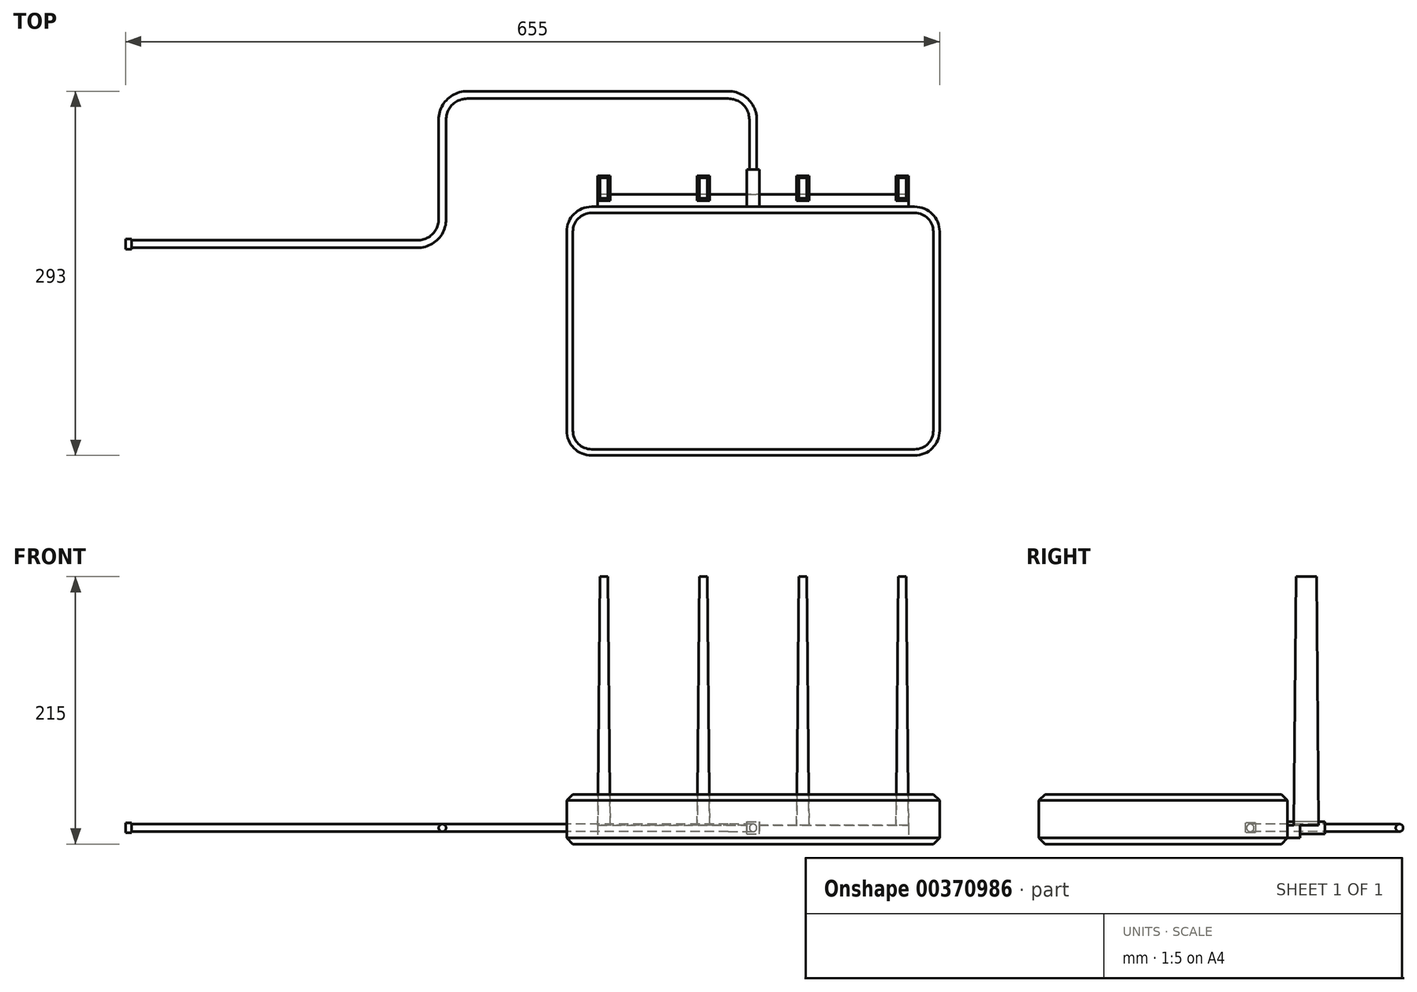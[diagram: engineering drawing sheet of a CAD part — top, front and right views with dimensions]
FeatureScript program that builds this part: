
annotation { "Feature Type Name" : "Feature", "Feature Type Description" : "" }
export const myFeature = defineFeature(function(context is Context, id is Id, definition is map)
    precondition{}
    {
        {
            var Q0;
            Q0=qCreatedBy(makeId("Top.planeOp"),FACE);
            var sketch = newSketch(context, id + "F0", { "sketchPlane" : qUnion([Q0])});
            skLineSegment(sketch, "E0.bottom", {"start": v(-150, -100) * mm, "end": v(150, -100) * mm});
            skLineSegment(sketch, "E0.top", {"start": v(-150, 100) * mm, "end": v(150, 100) * mm});
            skLineSegment(sketch, "E0.left", {"start": v(-150, -100) * mm, "end": v(-150, 100) * mm});
            skLineSegment(sketch, "E0.right", {"start": v(150, -100) * mm, "end": v(150, 100) * mm});
            skPoint(sketch, "E0.middle", {"position": v(0, 0) * mm});
            skSolve(sketch);
        }
        {
            var Q0;
            Q0 = qSketchRegion(id + "F0", true);
            extrude(context, id + "F1", {"entities" : qUnion([Q0]), "depth" : 40 * mm});
        }
        {
            var Q0;
            Q0=makeQuery(id+"F1.opExtrude","SWEPT_EDGE",EDGE,{"disambiguationData":[OSD([sQuery(id+"F0.wireOp",EDGE,"E0.bottom"),sQuery(id+"F0.wireOp",EDGE,"E0.left")])]});
            var Q1;
            Q1=makeQuery(id+"F1.opExtrude","SWEPT_EDGE",EDGE,{"disambiguationData":[OSD([sQuery(id+"F0.wireOp",EDGE,"E0.bottom"),sQuery(id+"F0.wireOp",EDGE,"E0.right")])]});
            var Q2;
            Q2=makeQuery(id+"F1.opExtrude","SWEPT_EDGE",EDGE,{"disambiguationData":[OSD([sQuery(id+"F0.wireOp",EDGE,"E0.top"),sQuery(id+"F0.wireOp",EDGE,"E0.right")])]});
            var Q3;
            Q3=makeQuery(id+"F1.opExtrude","SWEPT_EDGE",EDGE,{"disambiguationData":[OSD([sQuery(id+"F0.wireOp",EDGE,"E0.top"),sQuery(id+"F0.wireOp",EDGE,"E0.left")])]});
            fillet(context, id + "F2", {"entities" : qUnion([Q0, Q1, Q2, Q3]), "radius" : 20 * mm, "tangentPropagation" : true, "allowEdgeOverflow" : false});
        }
        {
            var Q0;
            Q0=makeQuery(id+"F1.opExtrude","CAP_EDGE",EDGE,{"disambiguationData":[OSD([sQuery(id+"F0.wireOp",EDGE,"E0.bottom")])],"isStart":false});
            var Q1;
            Q1=makeQuery(id+"F1.opExtrude","CAP_EDGE",EDGE,{"disambiguationData":[OSD([sQuery(id+"F0.wireOp",EDGE,"E0.bottom")])],"isStart":true});
            chamfer(context, id + "F3", {"entities" : qUnion([Q0, Q1]), "width" : 5 * mm, "tangentPropagation" : true});
        }
        {
            var Q0;
            Q0=qCreatedBy(makeId("Right.planeOp"),FACE);
            var sketch = newSketch(context, id + "F4", { "sketchPlane" : qUnion([Q0])});
            skLineSegment(sketch, "E1.bottom", {"start": v(90, 15) * mm, "end": v(110, 15) * mm});
            skLineSegment(sketch, "E1.top", {"start": v(90, 5) * mm, "end": v(110, 5) * mm});
            skLineSegment(sketch, "E1.left", {"start": v(90, 15) * mm, "end": v(90, 5) * mm});
            skLineSegment(sketch, "E1.right", {"start": v(110, 15) * mm, "end": v(110, 5) * mm});
            skSolve(sketch);
        }
        {
            var Q0;
            Q0 = qSketchRegion(id + "F4", true);
            extrude(context, id + "F5", {"entities" : qUnion([Q0]), "operationType" : NewBodyOperationType.ADD, "endBound" : BoundingType.SYMMETRIC, "depth" : 250 * mm});
        }
        {
            var Q0;
            Q0=makeQuery(id+"F5.opExtrude","SWEPT_FACE",FACE,{"disambiguationData":[OSD([sQuery(id+"F4.wireOp",EDGE,"E1.bottom")])]});
            var sketch = newSketch(context, id + "F6", { "sketchPlane" : qUnion([Q0])});
            skLineSegment(sketch, "E2.bottom", {"start": v(-125, 105) * mm, "end": v(-115, 105) * mm});
            skLineSegment(sketch, "E2.top", {"start": v(-125, 125) * mm, "end": v(-115, 125) * mm});
            skLineSegment(sketch, "E2.left", {"start": v(-125, 105) * mm, "end": v(-125, 125) * mm});
            skLineSegment(sketch, "E2.right", {"start": v(-115, 105) * mm, "end": v(-115, 125) * mm});
            skLineSegment(sketch, "E3.1.0.0", {"start": v(-35, 105) * mm, "end": v(-35, 125) * mm});
            skLineSegment(sketch, "E3.1.0.1", {"start": v(-45, 105) * mm, "end": v(-35, 105) * mm});
            skLineSegment(sketch, "E3.1.0.2", {"start": v(-45, 105) * mm, "end": v(-45, 125) * mm});
            skLineSegment(sketch, "E3.1.0.3", {"start": v(-45, 125) * mm, "end": v(-35, 125) * mm});
            skLineSegment(sketch, "E3.2.0.0", {"start": v(45, 105) * mm, "end": v(45, 125) * mm});
            skLineSegment(sketch, "E3.2.0.1", {"start": v(35, 105) * mm, "end": v(45, 105) * mm});
            skLineSegment(sketch, "E3.2.0.2", {"start": v(35, 105) * mm, "end": v(35, 125) * mm});
            skLineSegment(sketch, "E3.2.0.3", {"start": v(35, 125) * mm, "end": v(45, 125) * mm});
            skLineSegment(sketch, "E3.3.0.0", {"start": v(125, 105) * mm, "end": v(125, 125) * mm});
            skLineSegment(sketch, "E3.3.0.1", {"start": v(115, 105) * mm, "end": v(125, 105) * mm});
            skLineSegment(sketch, "E3.3.0.2", {"start": v(115, 105) * mm, "end": v(115, 125) * mm});
            skLineSegment(sketch, "E3.3.0.3", {"start": v(115, 125) * mm, "end": v(125, 125) * mm});
            skLineSegment(sketch, "E3.direction1", {"start": v(-125, 105) * mm, "end": v(-45, 105) * mm, "construction": true});
            skSolve(sketch);
        }
        {
            var Q0;
            Q0 = qSketchRegion(id + "F6", true);
            extrude(context, id + "F7", {"entities" : qUnion([Q0]), "operationType" : NewBodyOperationType.ADD, "depth" : 200 * mm, "hasDraft" : true, "draftAngle" : 0.5 * degree, "draftPullDirection" : true});
        }
        {
            var Q0;
            Q0=makeQuery(id+"F5.opExtrude","SWEPT_FACE",FACE,{"disambiguationData":[OSD([sQuery(id+"F4.wireOp",EDGE,"E1.right")])]});
            var sketch = newSketch(context, id + "F8", { "sketchPlane" : qUnion([Q0])});
            skLineSegment(sketch, "E4.bottom", {"start": v(-5, 18) * mm, "end": v(5, 18) * mm});
            skLineSegment(sketch, "E4.top", {"start": v(-5, 8) * mm, "end": v(5, 8) * mm});
            skLineSegment(sketch, "E4.left", {"start": v(-5, 18) * mm, "end": v(-5, 8) * mm});
            skLineSegment(sketch, "E4.right", {"start": v(5, 18) * mm, "end": v(5, 8) * mm});
            skSolve(sketch);
        }
        {
            var Q0;
            Q0 = qSketchRegion(id + "F8", true);
            extrude(context, id + "F9", {"entities" : qUnion([Q0]), "operationType" : NewBodyOperationType.ADD, "endBound" : BoundingType.SYMMETRIC, "depth" : 40 * mm});
        }
        {
            var Q0;
            Q0=makeQuery(id+"F9.opExtrude","CAP_FACE",FACE,{"disambiguationData":[OSD([sQuery(id+"F8.wireOp",EDGE,"E4.bottom"),sQuery(id+"F8.wireOp",EDGE,"E4.top"),sQuery(id+"F8.wireOp",EDGE,"E4.left"),sQuery(id+"F8.wireOp",EDGE,"E4.right")])],"isStart":false});
            var sketch = newSketch(context, id + "F10", { "sketchPlane" : qUnion([Q0])});
            skCircle(sketch, "E5", {"center": v(0, 13) * mm, "radius": 3 * mm});
            skSolve(sketch);
        }
        {
            var Q0;
            Q0=sQuery(id+"F10.wireOp",EDGE,"E5");
            cPlane(context, id + "F11", {"entities" : qUnion([Q0]), "cplaneType" : CPlaneType.LINE_ANGLE, "offset" : 25 * mm, "angle" : 0 * degree, "width" : 150 * mm, "height" : 150 * mm});
        }
        {
            var Q0;
            Q0=qCreatedBy(id+"F11.planeOp",FACE);
            var sketch = newSketch(context, id + "F12", { "sketchPlane" : qUnion([Q0])});
            skPoint(sketch, "E6.0", {"position": v(0, 130) * mm});
            skLineSegment(sketch, "E7", {"start": v(0, 130) * mm, "end": v(0, 150) * mm});
            skPoint(sketch, "E8.visualSharp", {"position": v(0, 210) * mm});
            skLineSegment(sketch, "E9", {"start": v(-270, 70) * mm, "end": v(-500, 70) * mm});
            skPoint(sketch, "E10.visualSharp", {"position": v(0, 70) * mm});
            skLineSegment(sketch, "E11", {"start": v(-250, 90) * mm, "end": v(-250, 170) * mm});
            skLineSegment(sketch, "E12", {"start": v(-230, 190) * mm, "end": v(-20, 190) * mm});
            skLineSegment(sketch, "E13", {"start": v(0, 170) * mm, "end": v(0, 150) * mm});
            skPoint(sketch, "E14.visualSharp", {"position": v(-250, 190) * mm});
            skArc(sketch, "E14.filletArc", {"start": v(-230, 190) * mm, "mid": v(-244.14, 184.14) * mm, "end": v(-250, 170) * mm});
            skPoint(sketch, "E15.visualSharp", {"position": v(0, 190) * mm});
            skArc(sketch, "E15.filletArc", {"start": v(0, 170) * mm, "mid": v(-5.86, 184.14) * mm, "end": v(-20, 190) * mm});
            skPoint(sketch, "E16.visualSharp", {"position": v(-250, 70) * mm});
            skArc(sketch, "E16.filletArc", {"start": v(-270, 70) * mm, "mid": v(-255.86, 75.86) * mm, "end": v(-250, 90) * mm});
            skSolve(sketch);
        }
        {
            var Q0;
            Q0 = qSketchRegion(id + "F10", true);
            var Q1;
            Q1 = qConstructionFilter(qBodyType(qCreatedBy(id + "F12" ,EDGE), BodyType.WIRE), ConstructionObject.NO);
            sweep(context, id + "F13", {"operationType" : NewBodyOperationType.ADD, "profiles" : qUnion([Q0]), "path" : qUnion([Q1])});
        }
        {
            var Q0;
            Q0=makeQuery(id+"F13.opSweep","CAP_FACE",FACE,{"disambiguationData":[OSD([sQuery(id+"F10.wireOp",EDGE,"E5"),sQuery(id+"F12.wireOp",VERTEX,"E9.end")])],"isStart":false});
            var sketch = newSketch(context, id + "F14", { "sketchPlane" : qUnion([Q0])});
            skLineSegment(sketch, "E17.bottom", {"start": v(-74, 17) * mm, "end": v(-66, 17) * mm});
            skLineSegment(sketch, "E17.top", {"start": v(-74, 9) * mm, "end": v(-66, 9) * mm});
            skLineSegment(sketch, "E17.left", {"start": v(-74, 17) * mm, "end": v(-74, 9) * mm});
            skLineSegment(sketch, "E17.right", {"start": v(-66, 17) * mm, "end": v(-66, 9) * mm});
            skPoint(sketch, "E17.middle", {"position": v(-70, 13) * mm});
            skSolve(sketch);
        }
        {
            var Q0;
            Q0 = qSketchRegion(id + "F14", true);
            extrude(context, id + "F15", {"entities" : qUnion([Q0]), "operationType" : NewBodyOperationType.ADD, "depth" : 5 * mm});
        }
    });
